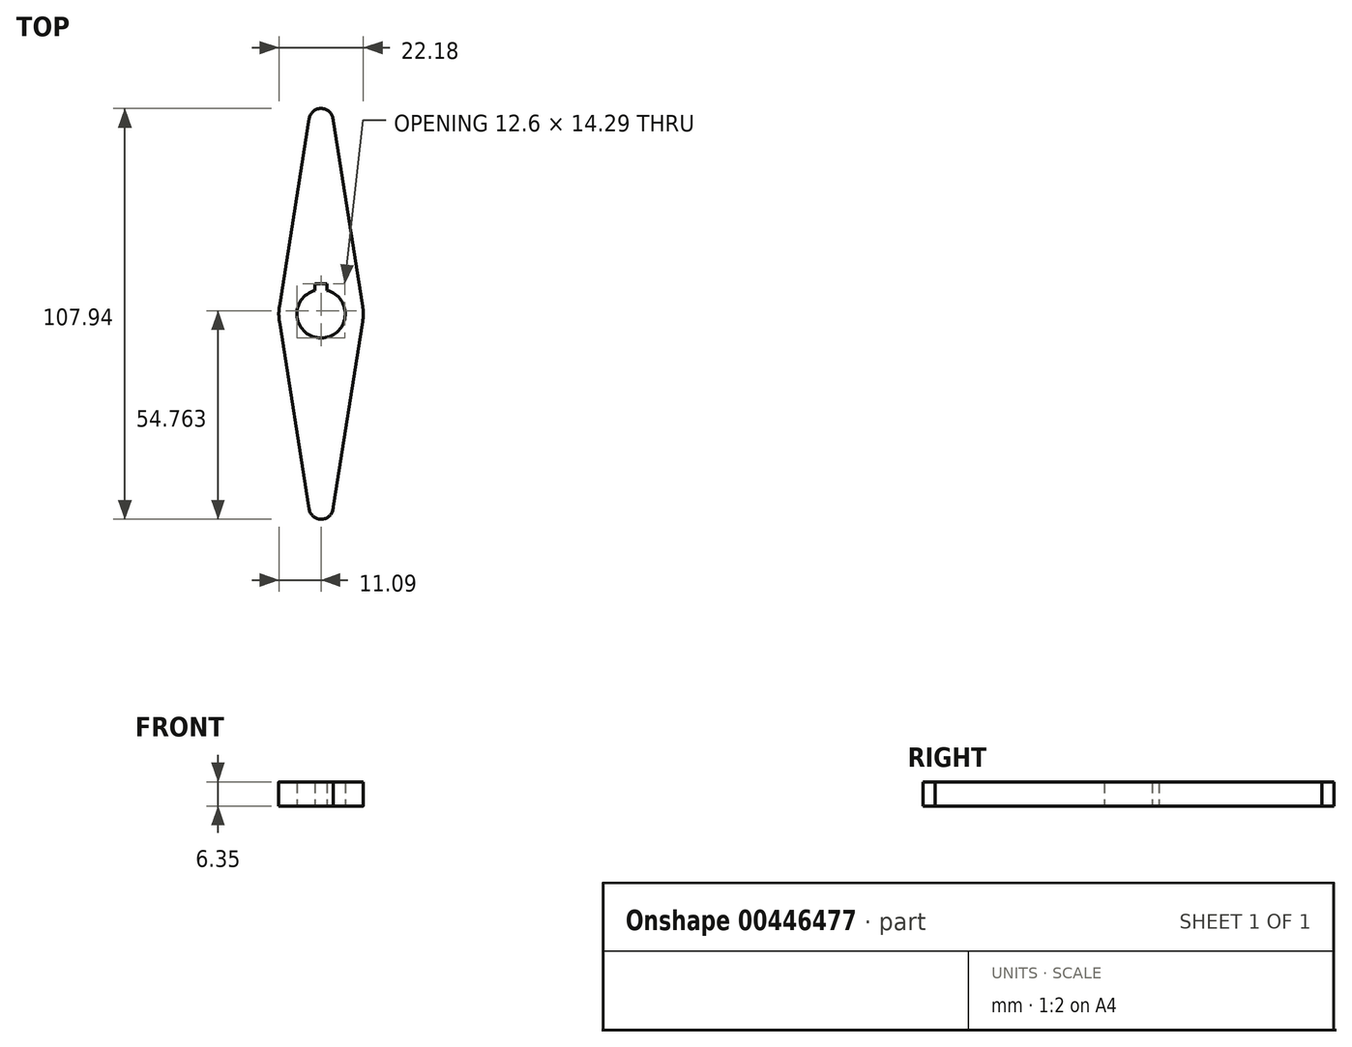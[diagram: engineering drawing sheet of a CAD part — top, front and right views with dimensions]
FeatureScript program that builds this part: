
annotation { "Feature Type Name" : "Feature", "Feature Type Description" : "" }
export const myFeature = defineFeature(function(context is Context, id is Id, definition is map)
    precondition{}
    {
        {
            var Q0;
            Q0=qCreatedBy(makeId("Top.planeOp"),FACE);
            var sketch = newSketch(context, id + "F0", { "sketchPlane" : qUnion([Q0])});
            skCircle(sketch, "E0", {"center": v(0, 0) * mm, "radius": 11.11 * mm});
            skCircle(sketch, "E1", {"center": v(0, 50.8) * mm, "radius": 3.18 * mm});
            skCircle(sketch, "E2", {"center": v(0, -50.8) * mm, "radius": 3.18 * mm});
            skLineSegment(sketch, "E3", {"start": v(-3.14, 51.3) * mm, "end": v(-11.25, 0) * mm});
            skLineSegment(sketch, "E4", {"start": v(-11.25, 0) * mm, "end": v(-3.14, -51.3) * mm});
            skLineSegment(sketch, "E5", {"start": v(3.17, 50.8) * mm, "end": v(11.25, 0) * mm});
            skLineSegment(sketch, "E6", {"start": v(11.25, 0) * mm, "end": v(3.18, -50.8) * mm});
            skPoint(sketch, "E7.0.midPoint", {"position": v(-5.5, 3.17) * mm});
            skArc(sketch, "E8", {"start": v(-1.59, 6.15) * mm, "mid": v(0, -6.35) * mm, "end": v(1.59, 6.15) * mm});
            skLineSegment(sketch, "E9.top", {"start": v(-1.59, 7.94) * mm, "end": v(1.59, 7.94) * mm});
            skLineSegment(sketch, "E9.left", {"start": v(-1.59, 6.15) * mm, "end": v(-1.59, 7.94) * mm});
            skLineSegment(sketch, "E9.right", {"start": v(1.59, 6.15) * mm, "end": v(1.59, 7.94) * mm});
            skPoint(sketch, "E9.middle", {"position": v(0, 7.04) * mm});
            skSolve(sketch);
        }
        {
            var Q0;
            Q0 = qSketchRegion(id + "F0", true);
            extrude(context, id + "F1", {"entities" : qUnion([Q0]), "depth" : 6.35 * mm, "offsetDistance" : 25.4 * mm});
        }
        {
            var Q0;
            Q0=makeQuery(id+"F1.opExtrude","SWEPT_EDGE",EDGE,{"disambiguationData":[OSD([sQuery(id+"F0.wireOp",EDGE,"E3"),sQuery(id+"F0.wireOp",EDGE,"E4")])]});
            var Q1;
            Q1=makeQuery(id+"F1.opExtrude","SWEPT_EDGE",EDGE,{"disambiguationData":[OSD([sQuery(id+"F0.wireOp",EDGE,"E5"),sQuery(id+"F0.wireOp",EDGE,"E6")])]});
            fillet(context, id + "F2", {"entities" : qUnion([Q0, Q1]), "radius" : 12.7 * mm, "tangentPropagation" : true, "allowEdgeOverflow" : false});
        }
    });
